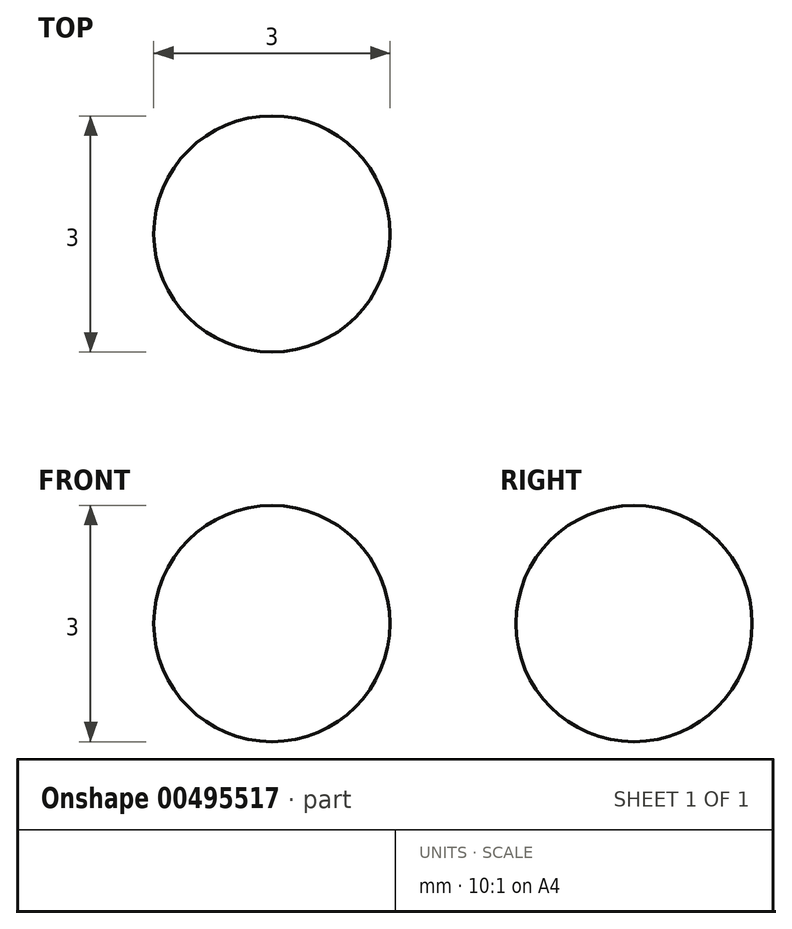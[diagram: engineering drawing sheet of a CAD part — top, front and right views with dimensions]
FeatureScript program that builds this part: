
annotation { "Feature Type Name" : "Feature", "Feature Type Description" : "" }
export const myFeature = defineFeature(function(context is Context, id is Id, definition is map)
    precondition{}
    {
        {
            var Q0;
            Q0=qCreatedBy(makeId("Front.planeOp"),FACE);
            var sketch = newSketch(context, id + "F0", { "sketchPlane" : qUnion([Q0])});
            skArc(sketch, "E0", {"start": v(0, 10) * mm, "mid": v(1.5, 11.5) * mm, "end": v(0, 13) * mm});
            skLineSegment(sketch, "E1", {"start": v(0, 13) * mm, "end": v(0, 10) * mm});
            skSolve(sketch);
        }
        {
            var Q0;
            Q0=qSketchRegion(id+"F0",true);
            var Q1;
            Q1=sQuery(id+"F0.wireOp",EDGE,"E1");
            revolve(context, id + "F1", {"entities" : qUnion([Q0]), "axis" : qUnion([Q1]), "revolveType" : RevolveType.FULL});
        }
    });
